# Revit family: Window-skylight-VELUX_AU_VSS-deck_mounted-solar-venting
name_source: partatom
category: Windows
units: mm (PartAtom-declared; Revit-internal decimal feet)

## family parameters
Always vertical = No
Cut with Voids When Loaded = No
Host = Roof
OmniClass Number = 23.30.30.14
OmniClass Title = Unit Skylights
Room Calculation Point = No
Shared = No

## types (10) — shared parameters
Analytic Construction = <None>
Assembly Code = B3020110
Deck Seal Mounting System = Steel - Anti-corrosive coating
Description = Solar powered top-hung skylight
Frame finish = Aluminum - Lacquered - Kynar 500 top finish - Neutral Gray
Glazing material = Glass-VELUX-Laminated
Heat Transfer Coefficient (U) = 0.1 BTU/(h·ft²·°F)
Manufacturer = VELUX
Maximum Roof Pitch = 90 degrees
Minimum Roof Pitch = 15 degrees
Model = VSS
Technical Drawings URL = http://www.velux.com.au
Technical Product Data URL = http://www.velux.com.au
Thermal Resistance (R) = 10.0000 (h·ft²·°F)/BTU
Type Comments = Designed for pitched roof installations
URL = http://www.velux.com.au
VELUX Flashing systems = EDL flashing, EDW flashing, EKW combi-flashing
VELUX Flashing systems URL = http://www.velux.com.au
VELUX Glazing options = Laminated (04)
VELUX Glazing options URL = http://www.velux.com.au
zero-valued in all types: Solar Heat Gain Coefficient, Visual Light Transmittance

## per-type parameters (varying)
| type | Frame and sash | Height | Operation | Rough Height | Rough Width | Width |
| C01 | Aluminum - Lacquered - Kynar 500 top finish - Neutral Gray | 721 mm | Solar venting | 683 mm | 533 mm | 567 mm |
| C04 | Aluminum - Lacquered - Kynar 500 top finish - Neutral Gray | 1000 mm | Solar venting | 962 mm | 533 mm | 567 mm |
| C06 | Aluminum - Lacquered - Kynar 500 top finish - Neutral Gray | 1200 mm | Solar venting | 1162 mm | 533 mm | 567 mm |
| C08 | Aluminum - Lacquered - Kynar 500 top finish - Neutral Gray | 1421 mm | Solar venting | 1383 mm | 533 mm | 567 mm |
| M04 | Aluminum - Lacquered - Kynar 500 top finish - Neutral Gray | 1000 mm | Solar venting | 962 mm | 764 mm | 797 mm |
| M06 | Aluminum - Lacquered - Kynar 500 top finish - Neutral Gray | 1200 mm |  | 1162 mm | 764 mm | 797 mm |
| M08 | Wood - Ponderosa Pine - finished White | 1421 mm | Solar venting | 1383 mm | 764 mm | 797 mm |
| S01 | Aluminum - Lacquered - Kynar 500 top finish - Neutral Gray | 721 mm | Solar venting | 683 mm | 1124 mm | 1157 mm |
| S06 | Aluminum - Lacquered - Kynar 500 top finish - Neutral Gray | 1200 mm | Solar venting | 1162 mm | 1124 mm | 1157 mm |
| M02 | Wood - Ponderosa Pine - finished White | 800 mm | Solar venting | 762 mm  [stored 2.5 ft] | 764 mm | 799 mm |

note: [stored X ft] marks values corroborated as IEEE doubles in the binary element streams (Revit-internal decimal feet)
